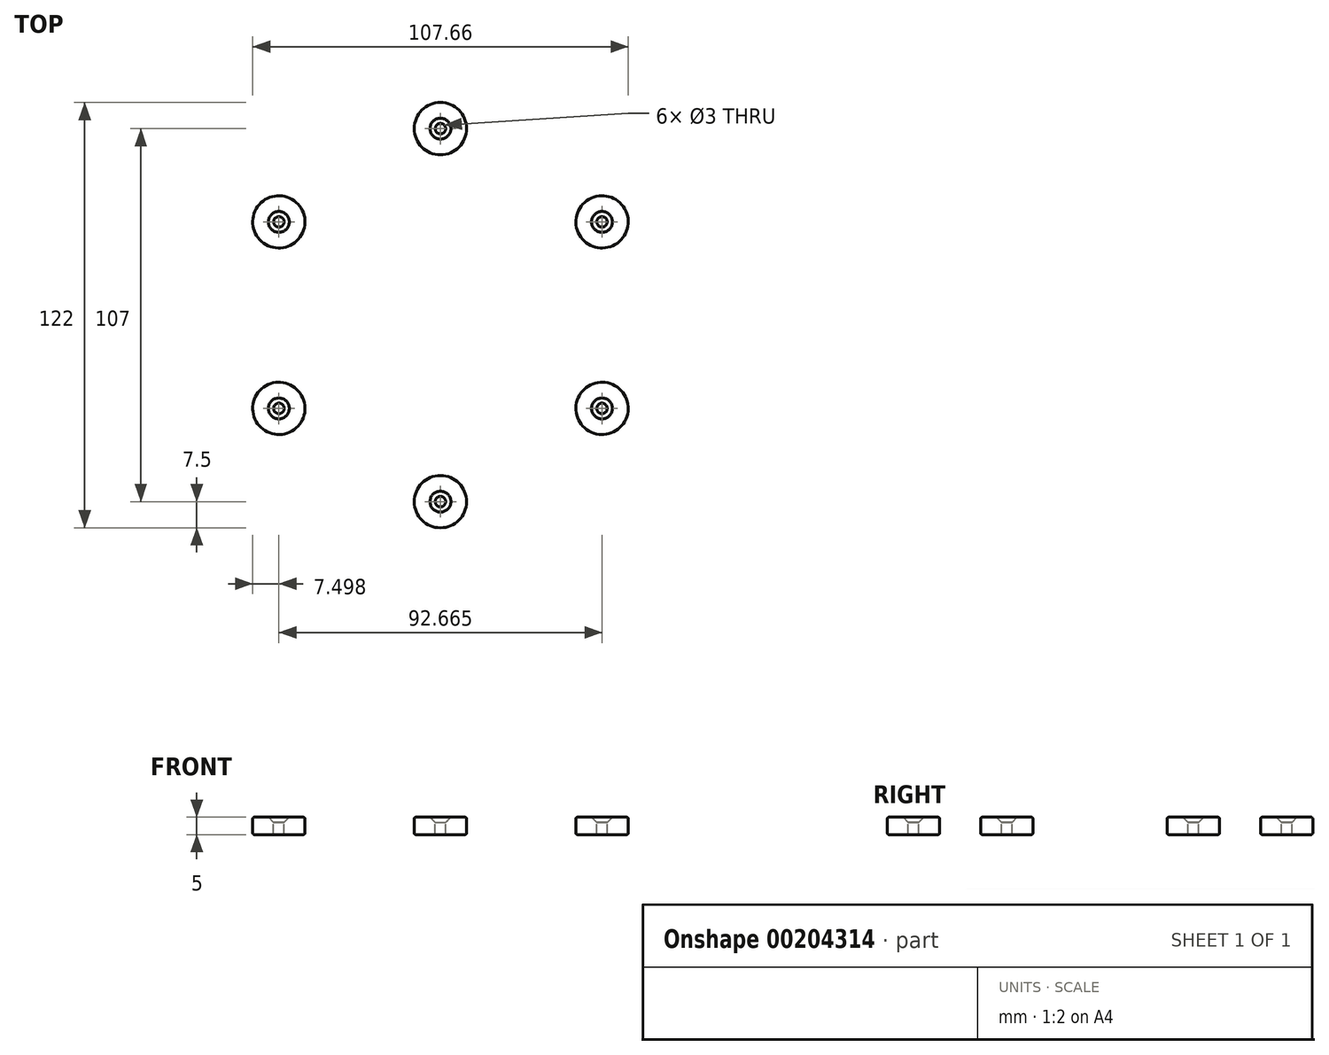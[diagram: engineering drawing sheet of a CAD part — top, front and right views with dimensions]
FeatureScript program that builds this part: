
annotation { "Feature Type Name" : "Feature", "Feature Type Description" : "" }
export const myFeature = defineFeature(function(context is Context, id is Id, definition is map)
    precondition{}
    {
        {
            assignVariable(context, id + "F0", {"name" : "magNUM", "anyValue" : 6});
        }
        {
            var Q0;
            Q0=qCreatedBy(makeId("Front.planeOp"),FACE);
            var sketch = newSketch(context, id + "F1", { "sketchPlane" : qUnion([Q0])});
            skLineSegment(sketch, "E0.bottom", {"start": v(0, 0) * mm, "end": v(-7.5, 0) * mm, "construction": true});
            skLineSegment(sketch, "E0.top", {"start": v(0, 5) * mm, "end": v(-7.5, 5) * mm, "construction": true});
            skLineSegment(sketch, "E0.left", {"start": v(0, 0) * mm, "end": v(0, 5) * mm, "construction": true});
            skLineSegment(sketch, "E0.right", {"start": v(-7.5, 0) * mm, "end": v(-7.5, 5) * mm, "construction": true});
            skLineSegment(sketch, "E1.bottom", {"start": v(0, 5) * mm, "end": v(-1.5, 5) * mm, "construction": true});
            skLineSegment(sketch, "E1.top", {"start": v(0, 0) * mm, "end": v(-1.5, 0) * mm, "construction": true});
            skLineSegment(sketch, "E1.left", {"start": v(0, 5) * mm, "end": v(0, 0) * mm, "construction": true});
            skLineSegment(sketch, "E1.right", {"start": v(-1.5, 5) * mm, "end": v(-1.5, 0) * mm, "construction": true});
            skLineSegment(sketch, "E2.bottom", {"start": v(-1.5, 5) * mm, "end": v(-3, 5) * mm, "construction": true});
            skLineSegment(sketch, "E2.top", {"start": v(-1.5, 3.5) * mm, "end": v(-3, 3.5) * mm, "construction": true});
            skLineSegment(sketch, "E2.left", {"start": v(-1.5, 5) * mm, "end": v(-1.5, 3.5) * mm, "construction": true});
            skLineSegment(sketch, "E2.right", {"start": v(-3, 5) * mm, "end": v(-3, 3.5) * mm, "construction": true});
            skLineSegment(sketch, "E3", {"start": v(-3, 5) * mm, "end": v(-1.5, 3.5) * mm});
            skLineSegment(sketch, "E4", {"start": v(-1.5, 3.5) * mm, "end": v(-1.5, 0) * mm});
            skLineSegment(sketch, "E5", {"start": v(-1.5, 0) * mm, "end": v(-7.5, 0) * mm});
            skLineSegment(sketch, "E6", {"start": v(-7.5, 0) * mm, "end": v(-7.5, 5) * mm});
            skLineSegment(sketch, "E7", {"start": v(-7.5, 5) * mm, "end": v(-3, 5) * mm});
            skSolve(sketch);
        }
        {
            var Q0;
            Q0=makeQuery(id+"F1.imprint","IMPRINT",FACE,{"disambiguationData":[TD([[makeQuery(id+"F1.imprint","IMPRINT",EDGE,{"derivedFrom":sQuery(id+"F1.wireOp",EDGE,"E3")}),-1.0]])]});
            var Q1;
            Q1=sQuery(id+"F1.wireOp",EDGE,"E1.left");
            revolve(context, id + "F2", {"entities" : qUnion([Q0]), "axis" : qUnion([Q1]), "revolveType" : RevolveType.FULL});
        }
        {
            var Q0;
            Q0=makeQuery(id+"F2.opRevolve","SWEPT_EDGE",EDGE,{"disambiguationData":[OSD([sQuery(id+"F1.wireOp",EDGE,"E6"),sQuery(id+"F1.wireOp",EDGE,"E7")])]});
            var Q1;
            Q1=makeQuery(id+"F2.opRevolve","SWEPT_EDGE",EDGE,{"disambiguationData":[OSD([sQuery(id+"F1.wireOp",EDGE,"E5"),sQuery(id+"F1.wireOp",EDGE,"E6")])]});
            fillet(context, id + "F3", {"entities" : qUnion([Q0, Q1]), "radius" : 0.5 * mm, "tangentPropagation" : true, "allowEdgeOverflow" : false});
        }
        {
            var Q0;
            Q0=qCreatedBy(makeId("Top.planeOp"),FACE);
            var sketch = newSketch(context, id + "F4", { "sketchPlane" : qUnion([Q0])});
            skLineSegment(sketch, "E8", {"start": v(0, 0) * mm, "end": v(0, -53.5) * mm, "construction": true});
            skCircle(sketch, "E9", {"center": v(0, -53.5) * mm, "radius": 60 * mm, "construction": true});
            skSolve(sketch);
        }
        {
            var Q0;
            Q0=makeQuery(id+"F2.opRevolve","SWEPT_BODY",BODY,{"disambiguationData":[OSD([sQuery(id+"F1.wireOp",EDGE,"E3"),sQuery(id+"F1.wireOp",EDGE,"E4"),sQuery(id+"F1.wireOp",EDGE,"E5"),sQuery(id+"F1.wireOp",EDGE,"E6"),sQuery(id+"F1.wireOp",EDGE,"E7")])]});
            var Q1;
            Q1=sQuery(id+"F4.wireOp",EDGE,"E9");
            circularPattern(context, id + "F5", {"entities" : qUnion([Q0]), "axis" : qUnion([Q1]), "angle" : 360 * degree, "instanceCount" : getVariable(context, 'magNUM'), "equalSpace" : true});
        }
    });
